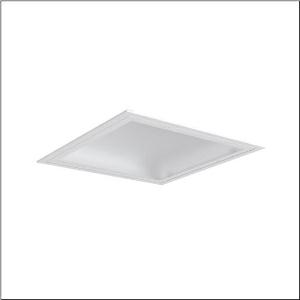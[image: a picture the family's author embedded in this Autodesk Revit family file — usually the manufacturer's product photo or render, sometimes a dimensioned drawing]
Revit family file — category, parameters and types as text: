
# Revit family: mira_r__21_51fr427a472a_c216
name_source: partatom
category: Lighting Fixtures
units: mm (PartAtom-declared; Revit-internal decimal feet)

## family parameters
Cut with Voids When Loaded = No
Host = Face
Light Source = No
Part Type = Normal
Room Calculation Point = No
Round Connector Dimension = Use Diameter
Shared = No

## types (1)
- Mira® 21 (1 x LED, 7680 lm, 66 W, 4000K)
    Apparent Load = 66 VA
    CIE Flux Codes = 50 81 97 100 100
    Color Rendering = 80
    Color Temperature = 4000K
    Default Elevation = 1800 mm
    Description = Mira® 21, clean room luminaire, primary light control with reflector, primary optical cover: cover, of PC, light emission: direct distribution, primary light characteristic: symmetric, installation type: recessed, LED, rated luminous flux: 7.680lm, luminous efficacy: 116lm/W, light colour: 840, colour temperature: 4000K, control gear: ECG, with terminal, 3-pole, max. 2.5mm², mains connection: 230V, AC, 50/60Hz, rated input power: 66W, luminaire housing, of sheet steel, coated, pure white (RAL 9010), with concealed spring brackets, module: M625, length: 623mm, width: 623mm, height: 115mm, protection rating (complete): IP54, insulation class (complete): insulation class I (protective earthing), certification: CE, UKCA, permissible operating ambient temperature: -5..+40°C, standard: EN 50419, packaging unit: 1 piece
    Height = 0 mm  [stored 0 ft]
    Lamp = 1 x LED
    Lamp Light Flux = 7680 lm
    Lamp Power = 66 W
    Lamp count = 1
    Length = 625 mm
    Luminous efficacy = 116 lm/W
    Manufacturer = Siteco
    ModVariant = No
    Model = 51FR427A472A
    Mounting Place = Ceiling
    Mounting Type = Recessed
    Number of Poles = 1
    OnlyDefault = Yes
    Power Factor = 1
    Product Name = Mira® 21
    Product group = clean room luminaire
    ProductGroupID = 402
    Protection Class = Protection class I
    Protection Degree = IP 54
    RLX_Detail_Level = 1
    RLX_Emergency_Light_Flux = 0 lm
    RLX_Emergency_Type = 0
    RLX_Emergency_Type_DB = No
    RlxData = <blob elided: 13369 chars, md5=50d37a39>
    Socket = socket
    Standby Power = 0 W
    System Light Flux = 7680 lm
    System Power = 66 W
    Type Comments = Product without accessories
    Type Image = l_1007109.jpg
    URL = http://relux.com
    VarID = ---
    Voltage = 0 V
    Weight = 0.00 kg
    Width = 625 mm

note: [stored X ft] marks values corroborated as IEEE doubles in the binary element streams (Revit-internal decimal feet)

## geometry (parser evidence)
native form markers: Sweep x10
no freeform markers — native parametric forms only
